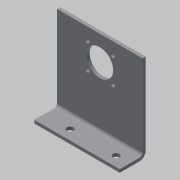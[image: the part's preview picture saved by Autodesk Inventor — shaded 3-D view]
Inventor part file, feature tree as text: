
AUTODESK INVENTOR PART (.ipt)
format: ipt  version: 2014 SP1 (Build 180222100, 222)  size: 124,928 bytes
history: native  units: in
note: dims shown in document units (in); Inventor stores cm internally (conversion verified against a paired STEP export)
features: sketch x5, sheet_metal_op x4, hole x3, other x2
ambient origin geometry x8: Origin, YZ Plane, XZ Plane, XY Plane, X Axis, Y Axis, Z Axis, Center Point
bodies: Solid1 (feature_tree)
feature tree (14):
  sheet_metal_op  "Face1"
  sheet_metal_op  "Flange1"
  hole  "Hole1"  [1 undecoded]
  hole  "Hole2"  [1 undecoded]
  hole  "Hole3"  [1 undecoded]
  sketch  "Sketch1"  dims[d0=3.292in d1=3.376in]
  other  "Plate1"
  sketch  "Sketch2"  dims[d2=0.12in d3=0.12in]
  other  "Plate2"
  sheet_metal_op  "Bend1"
  sheet_metal_op  "Corner1"
  sketch  "Sketch3"  dims[d4=0.06in d5=0.24in]
  sketch  "Sketch4"  dims[d6=0.12in]
  sketch  "Sketch5"  dims[d7=1.0in d8=90.0deg d9=0.12in d10=0.48in d11=0.12in d12=0.12in d13=2.413in d14=1.646in d15=1.028in d16=0.75in d17=0.375in d18=0.25in d19=0.5635in d20=0.12in d21=0.8108in d23=0.487in d24=0.487in d25=0.487in d26=0.487in d27=0.487in d28=0.487in d29=0.487in d30=0.487in d31=0.169in d32=0.75in d33=0.375in d34=0.25in d35=0.5635in d36=0.12in d37=0.8108in d39=1.0in d40=0.25in d41=0.75in d42=0.375in d43=0.25in d44=0.5635in d45=0.12in d46=0.8108in]
note: 3 required parameter values undecoded (feature->parameter linkage not recoverable at this tier; creation-order binding heuristic only, values carry confidence <= 0.55)
